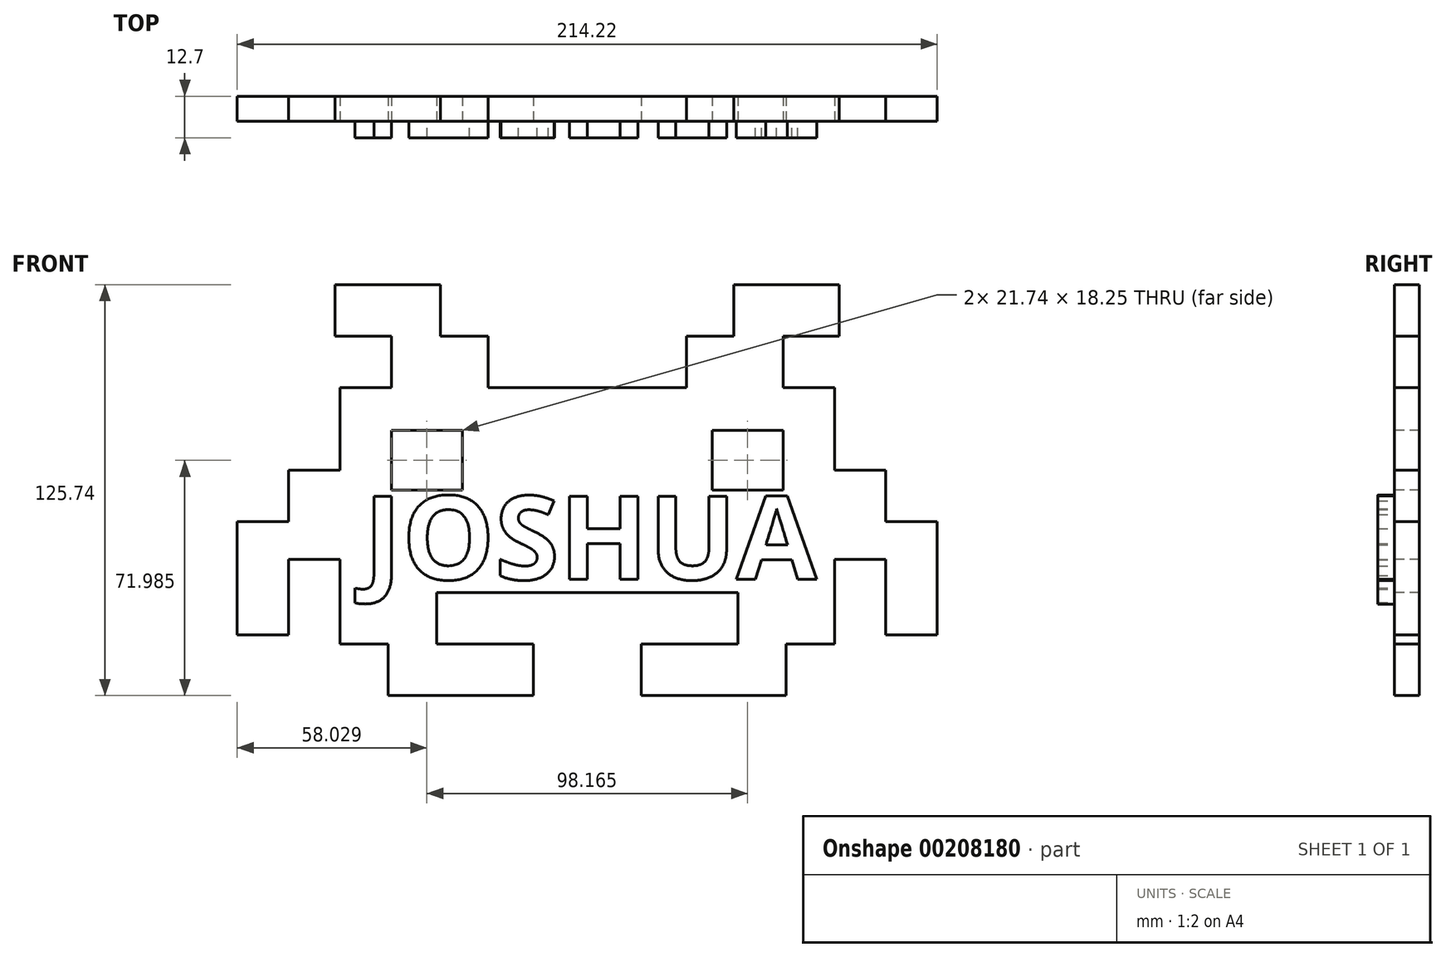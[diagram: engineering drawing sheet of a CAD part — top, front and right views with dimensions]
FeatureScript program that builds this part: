
annotation { "Feature Type Name" : "Feature", "Feature Type Description" : "" }
export const myFeature = defineFeature(function(context is Context, id is Id, definition is map)
    precondition{}
    {
        {
            var Q0;
            Q0=qCreatedBy(makeId("Front.planeOp"),FACE);
            var sketch = newSketch(context, id + "F1", { "sketchPlane" : qUnion([Q0])});
            skLineSegment(sketch, "E0.bottom", {"start": v(-31.44, 43.68) * mm, "end": v(74.6, 43.68) * mm});
            skLineSegment(sketch, "E0.left", {"start": v(-31.44, 43.68) * mm, "end": v(-31.44, -34.9) * mm});
            skLineSegment(sketch, "E0.right", {"start": v(119.9, 43.68) * mm, "end": v(119.9, -34.9) * mm});
            skText(sketch, "E1", { "text": "JOSHUA", "fontName": "OpenSans-Bold.ttf"});
            skLineSegment(sketch, "E2", {"start": v(112.72, -2.27) * mm, "end": v(119.9, -2.27) * mm});
            skPoint(sketch, "E2.endSnap0", {"position": v(119.9, 4.4) * mm});
            skPoint(sketch, "E2.endSnap1", {"position": v(112.72, -2.27) * mm});
            skLineSegment(sketch, "E3", {"start": v(-24.26, 3) * mm, "end": v(-31.44, 3) * mm});
            skLineSegment(sketch, "E4.bottom", {"start": v(-15.72, 27.96) * mm, "end": v(0, 27.96) * mm});
            skLineSegment(sketch, "E4.top", {"start": v(-15.72, 12.24) * mm, "end": v(0, 12.24) * mm});
            skLineSegment(sketch, "E4.left", {"start": v(-15.72, 27.96) * mm, "end": v(-15.72, 12.24) * mm});
            skLineSegment(sketch, "E4.right", {"start": v(0, 27.96) * mm, "end": v(0, 12.24) * mm});
            skLineSegment(sketch, "E5.bottom", {"start": v(88.46, 27.96) * mm, "end": v(104.18, 27.96) * mm});
            skLineSegment(sketch, "E5.top", {"start": v(88.46, 12.24) * mm, "end": v(104.18, 12.24) * mm});
            skLineSegment(sketch, "E5.left", {"start": v(88.46, 27.96) * mm, "end": v(88.46, 12.24) * mm});
            skLineSegment(sketch, "E5.right", {"start": v(104.18, 27.96) * mm, "end": v(104.18, 12.24) * mm});
            skLineSegment(sketch, "E6", {"start": v(44.23, 43.68) * mm, "end": v(44.23, 10.59) * mm, "construction": true});
            skLineSegment(sketch, "E7", {"start": v(0, 27.96) * mm, "end": v(44.23, 27.96) * mm, "construction": true});
            skLineSegment(sketch, "E8", {"start": v(44.23, 27.96) * mm, "end": v(88.46, 27.96) * mm, "construction": true});
            skLineSegment(sketch, "E9.bottom", {"start": v(119.9, 18.35) * mm, "end": v(135.62, 18.35) * mm});
            skLineSegment(sketch, "E9.top", {"start": v(119.9, -8.95) * mm, "end": v(135.62, -8.95) * mm});
            skLineSegment(sketch, "E9.left", {"start": v(119.9, 18.35) * mm, "end": v(119.9, -8.95) * mm});
            skLineSegment(sketch, "E10.bottom", {"start": v(135.62, 2.64) * mm, "end": v(151.34, 2.64) * mm});
            skLineSegment(sketch, "E10.top", {"start": v(135.62, -32.13) * mm, "end": v(151.34, -32.13) * mm});
            skLineSegment(sketch, "E10.left", {"start": v(135.62, -8.95) * mm, "end": v(135.62, -32.13) * mm});
            skLineSegment(sketch, "E11.top", {"start": v(105.1, -50.62) * mm, "end": v(60.72, -50.62) * mm});
            skLineSegment(sketch, "E11.right", {"start": v(60.72, -34.9) * mm, "end": v(60.72, -50.62) * mm});
            skLineSegment(sketch, "E12.left", {"start": v(74.6, 43.68) * mm, "end": v(74.6, 59.4) * mm});
            skLineSegment(sketch, "E12.right", {"start": v(104.18, 43.68) * mm, "end": v(104.18, 59.4) * mm});
            skLineSegment(sketch, "E13.bottom", {"start": v(104.18, 59.4) * mm, "end": v(121.4, 59.4) * mm});
            skLineSegment(sketch, "E14.top", {"start": v(121.4, 75.12) * mm, "end": v(89.1, 75.12) * mm});
            skLineSegment(sketch, "E14.left", {"start": v(121.4, 59.4) * mm, "end": v(121.4, 75.12) * mm});
            skLineSegment(sketch, "E14.right", {"start": v(89.1, 59.4) * mm, "end": v(89.1, 75.12) * mm});
            skLineSegment(sketch, "E15", {"start": v(135.62, 18.35) * mm, "end": v(135.62, 2.64) * mm});
            skLineSegment(sketch, "E16", {"start": v(89.1, 59.4) * mm, "end": v(74.6, 59.4) * mm});
            skLineSegment(sketch, "E17.bottom", {"start": v(44.23, -19.18) * mm, "end": v(90.3, -19.18) * mm});
            skLineSegment(sketch, "E17.top", {"start": v(60.72, -34.9) * mm, "end": v(90.3, -34.9) * mm});
            skLineSegment(sketch, "E17.left", {"start": v(44.23, -19.18) * mm, "end": v(44.23, -34.9) * mm});
            skLineSegment(sketch, "E17.right", {"start": v(90.3, -19.18) * mm, "end": v(90.3, -34.9) * mm});
            skLineSegment(sketch, "E18.trimOffspring", {"start": v(90.3, -34.9) * mm, "end": v(119.9, -34.9) * mm});
            skLineSegment(sketch, "E19.trimOffspring", {"start": v(104.18, 43.68) * mm, "end": v(119.9, 43.68) * mm});
            skLineSegment(sketch, "E20", {"start": v(74.6, 43.68) * mm, "end": v(104.18, 43.68) * mm});
            skLineSegment(sketch, "E21", {"start": v(105.1, -50.62) * mm, "end": v(105.1, -34.9) * mm});
            skLineSegment(sketch, "E22", {"start": v(88.46, 27.96) * mm, "end": v(88.46, 43.68) * mm, "construction": true});
            skLineSegment(sketch, "E23", {"start": v(135.62, -8.95) * mm, "end": v(151.34, -8.95) * mm, "construction": true});
            skLineSegment(sketch, "E24", {"start": v(151.34, -20.54) * mm, "end": v(135.62, -20.54) * mm, "construction": true});
            skLineSegment(sketch, "E25.trimOffspring", {"start": v(151.34, -20.54) * mm, "end": v(151.34, -32.13) * mm});
            skLineSegment(sketch, "E26", {"start": v(151.34, -8.95) * mm, "end": v(151.34, 2.64) * mm});
            skLineSegment(sketch, "E27", {"start": v(151.34, -8.95) * mm, "end": v(151.34, -20.54) * mm});
            skLineSegment(sketch, "E28", {"start": v(89.1, 59.4) * mm, "end": v(104.18, 59.4) * mm});
            skLineSegment(sketch, "E29.MirrorCS", {"start": v(-1.85, -34.9) * mm, "end": v(-31.44, -34.9) * mm});
            skLineSegment(sketch, "E30.MirrorCS", {"start": v(44.23, -19.18) * mm, "end": v(-1.85, -19.18) * mm});
            skLineSegment(sketch, "E31.MirrorCS", {"start": v(-1.85, -19.18) * mm, "end": v(-1.85, -34.9) * mm});
            skLineSegment(sketch, "E32.MirrorCS", {"start": v(-32.93, 75.12) * mm, "end": v(-0.64, 75.12) * mm});
            skLineSegment(sketch, "E33.MirrorCS", {"start": v(-0.64, 59.4) * mm, "end": v(-0.64, 75.12) * mm});
            skLineSegment(sketch, "E34.MirrorCS", {"start": v(-32.93, 59.4) * mm, "end": v(-32.93, 75.12) * mm});
            skLineSegment(sketch, "E35.MirrorCS", {"start": v(-15.72, 59.4) * mm, "end": v(-32.93, 59.4) * mm});
            skLineSegment(sketch, "E36.MirrorCS", {"start": v(-0.64, 59.4) * mm, "end": v(-15.72, 59.4) * mm});
            skLineSegment(sketch, "E37.MirrorCS", {"start": v(13.87, 43.68) * mm, "end": v(13.87, 59.4) * mm});
            skLineSegment(sketch, "E38.MirrorCS", {"start": v(-15.72, 43.68) * mm, "end": v(-15.72, 59.4) * mm});
            skLineSegment(sketch, "E39.MirrorCS", {"start": v(-31.44, 18.35) * mm, "end": v(-47.16, 18.35) * mm});
            skLineSegment(sketch, "E40.MirrorCS", {"start": v(-47.16, 18.35) * mm, "end": v(-47.16, 2.64) * mm});
            skLineSegment(sketch, "E41.MirrorCS", {"start": v(-47.16, 2.64) * mm, "end": v(-62.88, 2.64) * mm});
            skLineSegment(sketch, "E42.MirrorCS", {"start": v(-62.88, -8.95) * mm, "end": v(-62.88, 2.64) * mm});
            skLineSegment(sketch, "E43.MirrorCS", {"start": v(-62.88, -8.95) * mm, "end": v(-62.88, -20.54) * mm});
            skLineSegment(sketch, "E44.MirrorCS", {"start": v(-62.88, -20.54) * mm, "end": v(-62.88, -32.13) * mm});
            skLineSegment(sketch, "E45.MirrorCS", {"start": v(-47.16, -32.13) * mm, "end": v(-62.88, -32.13) * mm});
            skLineSegment(sketch, "E46.MirrorCS", {"start": v(-47.16, -8.95) * mm, "end": v(-47.16, -32.13) * mm});
            skLineSegment(sketch, "E47.MirrorCS", {"start": v(-31.44, -8.95) * mm, "end": v(-47.16, -8.95) * mm});
            skLineSegment(sketch, "E48.MirrorCS", {"start": v(-16.64, -50.62) * mm, "end": v(-16.64, -34.9) * mm});
            skLineSegment(sketch, "E49.MirrorCS", {"start": v(-16.64, -50.62) * mm, "end": v(27.74, -50.62) * mm});
            skLineSegment(sketch, "E50.MirrorCS", {"start": v(27.74, -34.9) * mm, "end": v(27.74, -50.62) * mm});
            skLineSegment(sketch, "E51.MirrorCS", {"start": v(27.74, -34.9) * mm, "end": v(-1.85, -34.9) * mm});
            skLineSegment(sketch, "E52", {"start": v(-0.64, 59.4) * mm, "end": v(13.87, 59.4) * mm});
            skLineSegment(sketch, "E53.bottom", {"start": v(104.18, 12.24) * mm, "end": v(82.45, 12.24) * mm});
            skLineSegment(sketch, "E53.top", {"start": v(104.18, 30.49) * mm, "end": v(82.45, 30.49) * mm});
            skLineSegment(sketch, "E53.left", {"start": v(104.18, 12.24) * mm, "end": v(104.18, 30.49) * mm});
            skLineSegment(sketch, "E53.right", {"start": v(82.45, 12.24) * mm, "end": v(82.45, 30.49) * mm});
            skLineSegment(sketch, "E54.MirrorCS", {"start": v(6.02, 12.24) * mm, "end": v(6.02, 30.49) * mm});
            skLineSegment(sketch, "E55.MirrorCS", {"start": v(-15.72, 30.49) * mm, "end": v(6.02, 30.49) * mm});
            skLineSegment(sketch, "E56.MirrorCS", {"start": v(-15.72, 12.24) * mm, "end": v(6.02, 12.24) * mm});
            skLineSegment(sketch, "E57.MirrorCS", {"start": v(-15.72, 12.24) * mm, "end": v(-15.72, 30.49) * mm});
            const initialGuessFviRciFx443WngOvW_0  = {"E1": [-0.02426, -0.01512, 1, 0, 0.0257]};
            skSetInitialGuess(sketch, initialGuessFviRciFx443WngOvW_0);
            skSolve(sketch);
        }
        {
            var Q0;
            Q0=makeQuery(id+"F1.imprint","IMPRINT",FACE,{"disambiguationData":[TD([[makeQuery(id+"F1.imprint","IMPRINT",EDGE,{"derivedFrom":sQuery(id+"F1.wireOp",EDGE,"E1.sketch_text.stroke-0")}),-1.0]])]});
            var Q1;
            Q1=makeQuery(id+"F1.imprint","IMPRINT",FACE,{"disambiguationData":[TD([[makeQuery(id+"F1.imprint","IMPRINT",EDGE,{"derivedFrom":sQuery(id+"F1.wireOp",EDGE,"E1.sketch_text.stroke-10")}),-1.0]])]});
            var Q2;
            Q2=makeQuery(id+"F1.imprint","IMPRINT",FACE,{"disambiguationData":[TD([[makeQuery(id+"F1.imprint","IMPRINT",EDGE,{"derivedFrom":sQuery(id+"F1.wireOp",EDGE,"E1.sketch_text.stroke-26")}),-1.0]])]});
            var Q3;
            Q3=makeQuery(id+"F1.imprint","IMPRINT",FACE,{"disambiguationData":[TD([[makeQuery(id+"F1.imprint","IMPRINT",EDGE,{"derivedFrom":sQuery(id+"F1.wireOp",EDGE,"E1.sketch_text.stroke-51")}),-1.0]])]});
            var Q4;
            Q4=makeQuery(id+"F1.imprint","IMPRINT",FACE,{"disambiguationData":[TD([[makeQuery(id+"F1.imprint","IMPRINT",EDGE,{"derivedFrom":sQuery(id+"F1.wireOp",EDGE,"E1.sketch_text.stroke-63")}),-1.0]])]});
            var Q5;
            Q5=makeQuery(id+"F1.imprint","IMPRINT",FACE,{"disambiguationData":[TD([[makeQuery(id+"F1.imprint","IMPRINT",EDGE,{"derivedFrom":sQuery(id+"F1.wireOp",EDGE,"E1.sketch_text.stroke-77")}),-1.0]])]});
            var Q6;
            Q6=makeQuery(id+"F1.imprint","IMPRINT",FACE,{"disambiguationData":[TD([[makeQuery(id+"F1.imprint","IMPRINT",EDGE,{"derivedFrom":sQuery(id+"F1.wireOp",EDGE,"E1.sketch_text.stroke-79")}),-1.0]])]});
            extrude(context, id + "F2", {"entities" : qUnion([Q0, Q1, Q2, Q3, Q4, Q5, Q6]), "depth" : 5.08 * mm});
        }
        {
            var Q0;
            {var subQ3=sQuery(id+"F1.wireOp",EDGE,"E0.bottom");Q0=makeQuery(id+"F1.imprint","IMPRINT",FACE,{"disambiguationData":[TD([[makeQuery(id+"F1.imprint","IMPRINT",EDGE,{"derivedFrom":subQ3}),-1.0]])]});}
            var Q1;
            Q1=makeQuery(id+"F1.imprint","IMPRINT",FACE,{"disambiguationData":[TD([[makeQuery(id+"F1.imprint","IMPRINT",EDGE,{"derivedFrom":sQuery(id+"F1.wireOp",EDGE,"E1.sketch_text.stroke-77")}),-1.0]])]});
            var Q2;
            Q2=makeQuery(id+"F1.imprint","IMPRINT",FACE,{"disambiguationData":[TD([[makeQuery(id+"F1.imprint","IMPRINT",EDGE,{"derivedFrom":sQuery(id+"F1.wireOp",EDGE,"E1.sketch_text.stroke-85")}),1.0]])]});
            var Q3;
            Q3=makeQuery(id+"F1.imprint","IMPRINT",FACE,{"disambiguationData":[TD([[makeQuery(id+"F1.imprint","IMPRINT",EDGE,{"derivedFrom":sQuery(id+"F1.wireOp",EDGE,"E1.sketch_text.stroke-63")}),-1.0]])]});
            var Q4;
            Q4=makeQuery(id+"F1.imprint","IMPRINT",FACE,{"disambiguationData":[TD([[makeQuery(id+"F1.imprint","IMPRINT",EDGE,{"derivedFrom":sQuery(id+"F1.wireOp",EDGE,"E1.sketch_text.stroke-51")}),-1.0]])]});
            var Q5;
            Q5=makeQuery(id+"F1.imprint","IMPRINT",FACE,{"disambiguationData":[TD([[makeQuery(id+"F1.imprint","IMPRINT",EDGE,{"derivedFrom":sQuery(id+"F1.wireOp",EDGE,"E1.sketch_text.stroke-26")}),-1.0]])]});
            var Q6;
            Q6=makeQuery(id+"F1.imprint","IMPRINT",FACE,{"disambiguationData":[TD([[makeQuery(id+"F1.imprint","IMPRINT",EDGE,{"derivedFrom":sQuery(id+"F1.wireOp",EDGE,"E1.sketch_text.stroke-10")}),-1.0]])]});
            var Q7;
            Q7=makeQuery(id+"F1.imprint","IMPRINT",FACE,{"disambiguationData":[TD([[makeQuery(id+"F1.imprint","IMPRINT",EDGE,{"derivedFrom":sQuery(id+"F1.wireOp",EDGE,"E1.sketch_text.stroke-18")}),1.0]])]});
            var Q8;
            Q8=makeQuery(id+"F1.imprint","IMPRINT",FACE,{"disambiguationData":[TD([[makeQuery(id+"F1.imprint","IMPRINT",EDGE,{"derivedFrom":sQuery(id+"F1.wireOp",EDGE,"E1.sketch_text.stroke-0")}),-1.0]])]});
            var Q9;
            {var subQ1=sQuery(id+"F1.wireOp",EDGE,"E37.MirrorCS");Q9=makeQuery(id+"F1.imprint","IMPRINT",FACE,{"disambiguationData":[TD([[makeQuery(id+"F1.imprint","IMPRINT",EDGE,{"derivedFrom":subQ1}),1.0]])]});}
            var Q10;
            Q10=makeQuery(id+"F1.imprint","IMPRINT",FACE,{"disambiguationData":[TD([[makeQuery(id+"F1.imprint","IMPRINT",EDGE,{"derivedFrom":sQuery(id+"F1.wireOp",EDGE,"E32.MirrorCS")}),-1.0]])]});
            var Q11;
            Q11=makeQuery(id+"F1.imprint","IMPRINT",FACE,{"disambiguationData":[TD([[makeQuery(id+"F1.imprint","IMPRINT",EDGE,{"derivedFrom":sQuery(id+"F1.wireOp",EDGE,"E13.bottom")}),1.0]])]});
            var Q12;
            Q12=makeQuery(id+"F1.imprint","IMPRINT",FACE,{"disambiguationData":[TD([[makeQuery(id+"F1.imprint","IMPRINT",EDGE,{"derivedFrom":sQuery(id+"F1.wireOp",EDGE,"E12.left")}),-1.0]])]});
            var Q13;
            {var subQ4=sQuery(id+"F1.wireOp",EDGE,"E9.bottom");Q13=makeQuery(id+"F1.imprint","IMPRINT",FACE,{"disambiguationData":[TD([[makeQuery(id+"F1.imprint","IMPRINT",EDGE,{"derivedFrom":subQ4}),-1.0]])]});}
            var Q14;
            Q14=makeQuery(id+"F1.imprint","IMPRINT",FACE,{"disambiguationData":[TD([[makeQuery(id+"F1.imprint","IMPRINT",EDGE,{"derivedFrom":sQuery(id+"F1.wireOp",EDGE,"E11.top")}),-1.0]])]});
            var Q15;
            {var subQ0=sQuery(id+"F1.wireOp",EDGE,"E48.MirrorCS");Q15=makeQuery(id+"F1.imprint","IMPRINT",FACE,{"disambiguationData":[TD([[makeQuery(id+"F1.imprint","IMPRINT",EDGE,{"derivedFrom":subQ0}),-1.0]])]});}
            var Q16;
            {var subQ3=sQuery(id+"F1.wireOp",EDGE,"E39.MirrorCS");Q16=makeQuery(id+"F1.imprint","IMPRINT",FACE,{"disambiguationData":[TD([[makeQuery(id+"F1.imprint","IMPRINT",EDGE,{"derivedFrom":subQ3}),1.0]])]});}
            var Q17;
            Q17=makeQuery(id+"F1.imprint","IMPRINT",FACE,{"disambiguationData":[TD([[makeQuery(id+"F1.imprint","IMPRINT",EDGE,{"derivedFrom":sQuery(id+"F1.wireOp",EDGE,"E1.sketch_text.stroke-79")}),-1.0]])]});
            var Q18;
            Q18=makeQuery(id+"F1.imprint","IMPRINT",FACE,{"disambiguationData":[TD([[makeQuery(id+"F1.imprint","IMPRINT",EDGE,{"derivedFrom":sQuery(id+"F1.wireOp",EDGE,"E1.sketch_text.stroke-87")}),1.0]])]});
            extrude(context, id + "F0", {"entities" : qUnion([Q0, Q1, Q2, Q3, Q4, Q5, Q6, Q7, Q8, Q9, Q10, Q11, Q12, Q13, Q14, Q15, Q16, Q17, Q18]), "operationType" : NewBodyOperationType.ADD, "oppositeDirection" : true, "depth" : 7.62 * mm});
        }
    });
